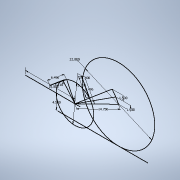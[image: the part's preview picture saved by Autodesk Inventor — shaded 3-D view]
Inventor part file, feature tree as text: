
AUTODESK INVENTOR PART (.ipt)
format: ipt  version: 2022 (Build 260153000, 153)  size: 105,472 bytes
history: native  units: in
note: dims shown in document units (in); Inventor stores cm internally (conversion verified against a paired STEP export)
features: sketch x1
ambient origin geometry x8: Origin, YZ Plane, XZ Plane, XY Plane, X Axis, Y Axis, Z Axis, Center Point
feature tree (1):
  sketch  "Sketch1"  dims[d1=15.0in d3=1.5in d4=1.5in d8=22.0in d10=14.75in d12=6.4961in d14=5.1181in d17=4.5in d21=11.4in d22=5.1181in d23=6.4961in]
